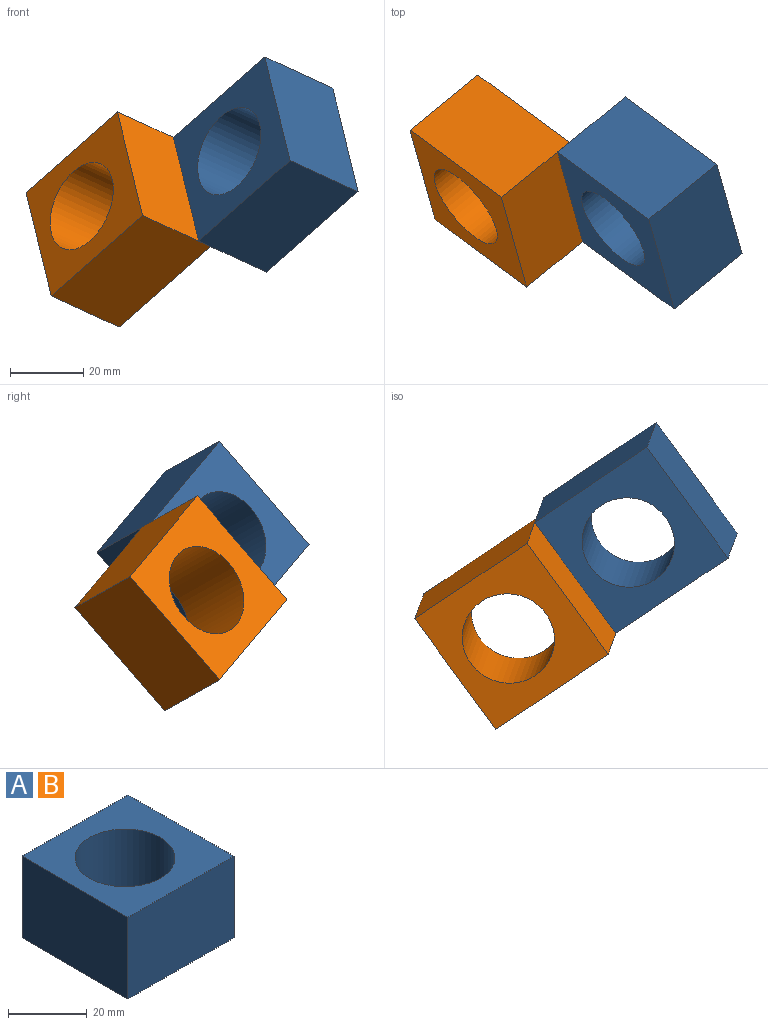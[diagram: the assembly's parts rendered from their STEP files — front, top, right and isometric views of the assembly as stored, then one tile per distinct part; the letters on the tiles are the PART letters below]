
ASSEMBLY  parts=2 mates=2
PART A: 7 faces, bbox 38.1x38.1x25.4 mm
  f0: plane 38.1x25.4mm, normal (0,1,0), area 967.7mm2, adj f1,f3,f4,f5
  f1: plane 38.1x25.4mm, normal (-1,0,0), area 967.7mm2, adj f0,f2,f4,f5
  f2: plane 38.1x25.4mm, normal (0,-1,0), area 967.7mm2, adj f1,f3,f4,f5
  f3: plane 38.1x25.4mm, normal (1,0,0), area 967.7mm2, adj f0,f2,f4,f5
  f4: plane 38.1x38.1mm, normal (0,0,1), area 944.9mm2, adj f0,f1,f2,f3,f6
  f5: plane 38.1x38.1mm, normal (0,0,-1), area 944.9mm2, adj f0,f1,f2,f3,f6
  f6: cylinder r=12.7mm len=25.4mm, axis (0,0,1), area 2026.8mm2, adj f4,f5
PART B: same geometry as A
PLACE A rot(axis=(0.71,-0.69,-0.16),71.5deg) t=(15.35,12.43,-7.01)mm
PLACE B rot(axis=(0.71,-0.69,-0.16),71.5deg) t=(-25.01,18.46,-22.03)mm
MATE planar B.f2 <-> A.f2  axis (0.18,-0.64,-0.74) through (-21.81,1.7,-6.77)mm
MATE planar B.f3 <-> A.f1  axis (0.66,-0.48,0.58) through (-12.75,4.72,18.43)mm
